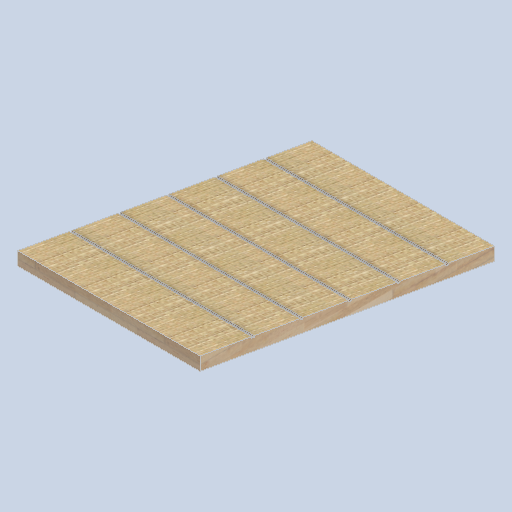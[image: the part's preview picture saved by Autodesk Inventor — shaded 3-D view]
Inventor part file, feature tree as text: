
AUTODESK INVENTOR PART (.ipt)
format: ipt  version: 2024.2 (Build 282272000, 272)  size: 254,464 bytes
history: native  units: in
note: dims shown in document units (in); Inventor stores cm internally (conversion verified against a paired STEP export)
features: sketch x5, other x3, plane x3
ambient origin geometry x8: Origin, YZ Plane, XZ Plane, XY Plane, X Axis, Y Axis, Z Axis, Center Point
bodies: Solid1 (feature_tree)
feature tree (11):
  other  "eave_panel_01.ipt"
  other  "Solid1::eave_panel_01.ipt"
  other  "TaggingFeature1"
  sketch  "Sketch1"  dims[d0=0.3937in]
  sketch  "Sketch2"
  sketch  "Sketch3"
  sketch  "Sketch4"
  sketch  "Sketch5"
  plane  "Work Plane1"
  plane  "Work Plane2"
  plane  "Work Plane3"
